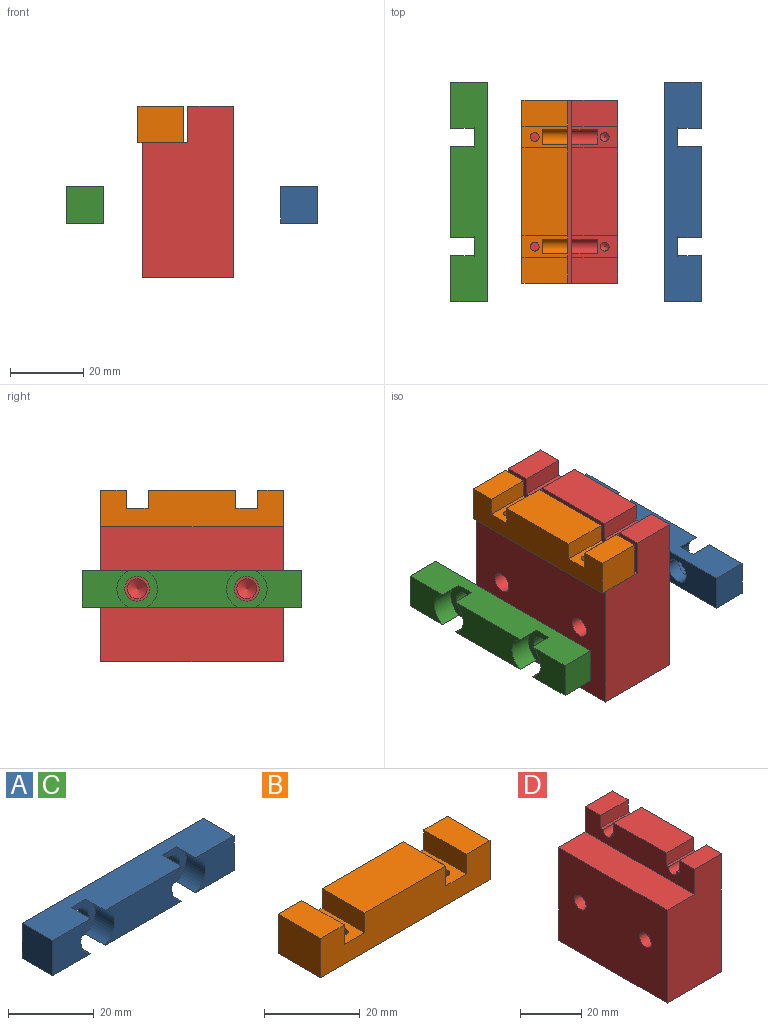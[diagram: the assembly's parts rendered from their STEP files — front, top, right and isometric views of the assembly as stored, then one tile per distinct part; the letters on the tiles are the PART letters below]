
ASSEMBLY  parts=4 mates=5
PART A: 16 faces, bbox 60x10x10 mm
  f0: plane 60x10mm, normal (0,0,-1), area 538.5mm2, adj f2,f3,f4,f5,f6,f7,f8,f9
  f1: plane 60x10mm, normal (0,0,1), area 538.5mm2, adj f2,f3,f4,f5,f6,f7,f8,f9
  f2: plane 12.58x10mm, normal (0,-1,0), area 103.3mm2, adj f0,f1,f5,f14
  f3: plane 25.15x10mm, normal (0,-1,0), area 206.6mm2, adj f0,f1,f10,f13
  f4: plane 12.58x10mm, normal (0,-1,0), area 103.3mm2, adj f0,f1,f6,f9
  f5: plane 10x10mm, normal (1,0,0), area 100mm2, adj f0,f1,f2,f7
  f6: plane 10x10mm, normal (-1,0,0), area 100mm2, adj f0,f1,f4,f7
  f7: plane 60x10mm, normal (0,1,0), area 528.3mm2, adj f0,f1,f5,f6,f11,f15
  f8: plane 11.11x10mm, normal (0,-1,0), area 57.5mm2, adj f0,f1,f9,f10,f11
  f9: cylinder r=5.56mm len=10mm, axis (0,-1,0), area 79mm2, adj f0,f1,f4,f8
  f10: cylinder r=5.56mm len=10mm, axis (0,-1,0), area 79mm2, adj f0,f1,f3,f8
  f11: cylinder r=3.38mm len=6.76mm, axis (0,-1,0), area 77.5mm2, adj f7,f8
  f12: plane 11.11x10mm, normal (0,-1,0), area 57.5mm2, adj f0,f1,f13,f14,f15
  f13: cylinder r=5.56mm len=10mm, axis (0,-1,0), area 79mm2, adj f0,f1,f3,f12
  f14: cylinder r=5.56mm len=10mm, axis (0,-1,0), area 79mm2, adj f0,f1,f2,f12
  f15: cylinder r=3.38mm len=6.76mm, axis (0,-1,0), area 77.5mm2, adj f7,f12
PART B: 20 faces, bbox 50x12.5x10 mm
  f0: plane 50x10mm, normal (0,1,0), area 427.4mm2, adj f1,f2,f3,f5,f6,f7,f8,f9
  f1: plane 12.5x6mm, normal (0,0,1), area 42.5mm2, adj f0,f4,f12,f13,f14,f15,f18
  f2: plane 12.5x7mm, normal (0,0,1), area 87.5mm2, adj f0,f4,f8,f12
  f3: plane 24x12.5mm, normal (0,0,1), area 300mm2, adj f0,f4,f9,f13
  f4: plane 50x10mm, normal (0,-1,0), area 440mm2, adj f1,f2,f3,f5,f6,f7,f8,f9
  f5: plane 50x12.5mm, normal (0,0,-1), area 616mm2, adj f0,f4,f6,f8,f18,f19
  f6: plane 12.5x10mm, normal (1,0,0), area 125mm2, adj f0,f4,f5,f7
  f7: plane 12.5x7mm, normal (0,0,1), area 87.5mm2, adj f0,f4,f6,f10
  f8: plane 12.5x10mm, normal (-1,0,0), area 125mm2, adj f0,f2,f4,f5
  f9: plane 12.5x5mm, normal (1,0,0), area 62.5mm2, adj f0,f3,f4,f11
  f10: plane 12.5x5mm, normal (-1,0,0), area 62.5mm2, adj f0,f4,f7,f11
  f11: plane 12.5x6mm, normal (0,0,1), area 42.5mm2, adj f0,f4,f9,f10,f16,f17,f19
  f12: plane 12.5x5mm, normal (1,0,0), area 62.5mm2, adj f0,f1,f2,f4
  f13: plane 12.5x5mm, normal (-1,0,0), area 62.5mm2, adj f0,f1,f3,f4
  f14: cylinder r=2mm len=7mm, axis (0,-1,0), area 44mm2, adj f0,f1,f15
  f15: plane 4x2mm, normal (0,1,0), area 6.3mm2, adj f1,f14
  f16: cylinder r=2mm len=7mm, axis (0,1,0), area 44mm2, adj f0,f11,f17
  f17: plane 4x2mm, normal (0,1,0), area 6.3mm2, adj f11,f16
  f18: cylinder r=1.2mm len=5mm, axis (0,0,1), area 37.7mm2, adj f1,f5
  f19: cylinder r=1.2mm len=5mm, axis (0,0,1), area 37.7mm2, adj f5,f11
PART C: same geometry as A
PART D: 32 faces, bbox 25x50x47 mm
  f0: plane 12.5x6mm, normal (0,0,1), area 42.5mm2, adj f4,f10,f20,f21,f26,f30,f31
  f1: plane 12.5x6mm, normal (0,0,1), area 42.5mm2, adj f4,f10,f22,f23,f24,f28,f29
  f2: plane 24x12.5mm, normal (0,0,1), area 300mm2, adj f4,f10,f21,f23
  f3: plane 12.5x7mm, normal (0,0,1), area 87.5mm2, adj f4,f6,f10,f20
  f4: plane 50x10mm, normal (-1,0,0), area 427.4mm2, adj f0,f1,f2,f3,f5,f6,f7,f19
  f5: plane 12.5x7mm, normal (0,0,1), area 87.5mm2, adj f4,f7,f10,f22
  f6: plane 47x25mm, normal (0,-1,0), area 1050mm2, adj f3,f4,f8,f9,f10,f19
  f7: plane 47x25mm, normal (0,1,0), area 1050mm2, adj f4,f5,f8,f9,f10,f19
  f8: plane 50x37mm, normal (-1,0,0), area 1804mm2, adj f6,f7,f9,f11,f13,f19
  f9: plane 50x25mm, normal (0,0,-1), area 1250mm2, adj f6,f7,f8,f10
  f10: plane 50x47mm, normal (1,0,0), area 2244mm2, adj f0,f1,f2,f3,f5,f6,f7,f9
  f11: cylinder r=2.71mm len=10mm, axis (-1,0,0), area 170mm2, adj f8,f12
  f12: cone r=0mm half-angle=59deg, axis (-1,0,0), area 26.8mm2, adj f11
  f13: cylinder r=2.71mm len=10mm, axis (-1,0,0), area 170mm2, adj f8,f14
  f14: cone r=0mm half-angle=59deg, axis (-1,0,0), area 26.8mm2, adj f13
  f15: cylinder r=2.71mm len=10mm, axis (1,0,0), area 170mm2, adj f10,f16
  f16: cone r=0mm half-angle=59deg, axis (1,0,0), area 26.8mm2, adj f15
  f17: cylinder r=2.71mm len=10mm, axis (1,0,0), area 170mm2, adj f10,f18
  f18: cone r=0mm half-angle=59deg, axis (1,0,0), area 26.8mm2, adj f17
  f19: plane 50x12.5mm, normal (0,0,1), area 625mm2, adj f4,f6,f7,f8
  f20: plane 12.5x5mm, normal (0,1,0), area 62.5mm2, adj f0,f3,f4,f10
  f21: plane 12.5x5mm, normal (0,-1,0), area 62.5mm2, adj f0,f2,f4,f10
  f22: plane 12.5x5mm, normal (0,-1,0), area 62.5mm2, adj f1,f4,f5,f10
  f23: plane 12.5x5mm, normal (0,1,0), area 62.5mm2, adj f1,f2,f4,f10
  f24: cylinder r=1.2mm len=10mm, axis (0,0,1), area 75.4mm2, adj f1,f25
  f25: cone r=0mm half-angle=59deg, axis (0,0,1), area 5.3mm2, adj f24
  f26: cylinder r=1.2mm len=10mm, axis (0,0,1), area 75.4mm2, adj f0,f27
  f27: cone r=0mm half-angle=59deg, axis (0,0,1), area 5.3mm2, adj f26
  f28: plane 4x2mm, normal (-1,0,0), area 6.3mm2, adj f1,f29
  f29: cylinder r=2mm len=7mm, axis (1,0,0), area 44mm2, adj f1,f4,f28
  f30: plane 4x2mm, normal (-1,0,0), area 6.3mm2, adj f0,f31
  f31: cylinder r=2mm len=7mm, axis (1,0,0), area 44mm2, adj f0,f4,f30
PLACE A rot(axis=(0,0,1),90deg) t=(35.38,0,0)mm
PLACE B rot(axis=(0,0,-1),90deg) t=(-1.14,0,22)mm
PLACE C rot(axis=(0.71,0.71,0),180deg) t=(-33.1,0,0)mm
PLACE D at identity fixed
MATE cylindrical C.f13 <-> D.f11  axis (-1,0,0) through (-26.75,15,0)mm
MATE slider D.f16 <-> A.f9  axis (1,0,0) through (12.5,-15,0)mm
MATE slider D.f29 <-> B.f14  axis (-1,0,0) through (0,15,22)mm
MATE slider A.f13 <-> D.f18  axis (-1,0,0) through (25.38,15,0)mm
MATE cylindrical C.f9 <-> D.f13  axis (1,0,0) through (-23.1,-15,0)mm
